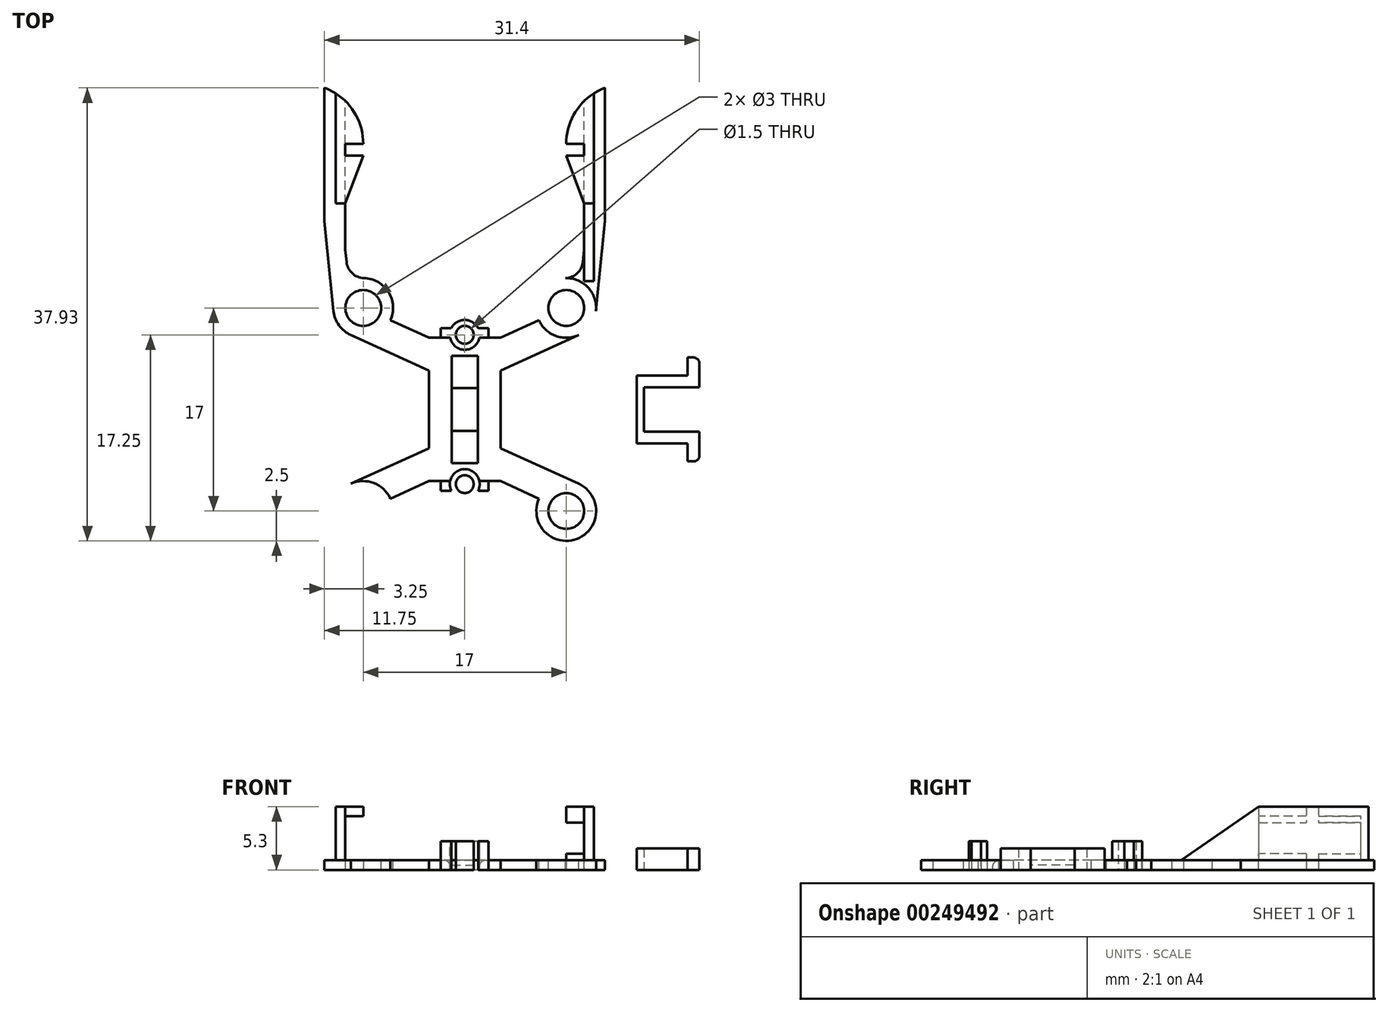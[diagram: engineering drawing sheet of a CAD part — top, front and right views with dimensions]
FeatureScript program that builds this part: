
annotation { "Feature Type Name" : "Feature", "Feature Type Description" : "" }
export const myFeature = defineFeature(function(context is Context, id is Id, definition is map)
    precondition{}
    {
        {
            var Q0;
            Q0=qCreatedBy(makeId("Top.planeOp"),FACE);
            var sketch = newSketch(context, id + "F0", { "sketchPlane" : qUnion([Q0])});
            skLineSegment(sketch, "E0", {"start": v(0, 24.7) * mm, "end": v(0, -21.3) * mm, "construction": true});
            skLineSegment(sketch, "E1", {"start": v(-15, 1.7) * mm, "end": v(15, 1.7) * mm, "construction": true});
            skCircle(sketch, "E2", {"center": v(0, 7.95) * mm, "radius": 1.25 * mm});
            skPoint(sketch, "E3", {"position": v(0, 1.7) * mm});
            skLineSegment(sketch, "E4.bottom", {"start": v(-8.5, 10.2) * mm, "end": v(8.5, 10.2) * mm, "construction": true});
            skLineSegment(sketch, "E4.top", {"start": v(-8.5, -6.8) * mm, "end": v(8.5, -6.8) * mm, "construction": true});
            skLineSegment(sketch, "E4.left", {"start": v(-8.5, 10.2) * mm, "end": v(-8.5, -6.8) * mm, "construction": true});
            skLineSegment(sketch, "E4.right", {"start": v(8.5, 10.2) * mm, "end": v(8.5, -6.8) * mm, "construction": true});
            skPoint(sketch, "E5.positionSnap0", {"position": v(0, 10.2) * mm});
            skPoint(sketch, "E5.positionSnap1", {"position": v(-8.5, 1.7) * mm});
            skArc(sketch, "E6", {"start": v(-6.22, 9.17) * mm, "mid": v(-9.38, 12.54) * mm, "end": v(-9.53, 7.92) * mm});
            skCircle(sketch, "E7", {"center": v(-8.5, 10.2) * mm, "radius": 1.5 * mm});
            skCircle(sketch, "E8", {"center": v(0, 7.95) * mm, "radius": 0.75 * mm});
            skLineSegment(sketch, "E9.bottom", {"start": v(-3, 7.7) * mm, "end": v(-1.22, 7.7) * mm});
            skLineSegment(sketch, "E9.top", {"start": v(-3, -4.3) * mm, "end": v(-1.22, -4.3) * mm});
            skLineSegment(sketch, "E9.left", {"start": v(-3, 4.95) * mm, "end": v(-3, -1.55) * mm});
            skLineSegment(sketch, "E9.right", {"start": v(3, 4.95) * mm, "end": v(3, -1.55) * mm});
            skPoint(sketch, "E10.positionSnap0", {"position": v(0, 7.7) * mm});
            skPoint(sketch, "E10.positionSnap1", {"position": v(-3, 1.7) * mm});
            skLineSegment(sketch, "E11", {"start": v(-9.53, 7.92) * mm, "end": v(-3, 4.95) * mm});
            skLineSegment(sketch, "E12.trimOffspring", {"start": v(-6.22, 9.17) * mm, "end": v(-3, 7.7) * mm});
            skLineSegment(sketch, "E13.trimOffspring", {"start": v(1.22, 7.7) * mm, "end": v(3, 7.7) * mm});
            skLineSegment(sketch, "E14.bottom", {"start": v(-1.1, 6.2) * mm, "end": v(1.1, 6.2) * mm});
            skLineSegment(sketch, "E14.top", {"start": v(-1.1, -2.8) * mm, "end": v(1.1, -2.8) * mm});
            skLineSegment(sketch, "E14.left", {"start": v(-1.1, 6.2) * mm, "end": v(-1.1, -2.8) * mm});
            skLineSegment(sketch, "E14.right", {"start": v(1.1, 6.2) * mm, "end": v(1.1, -2.8) * mm});
            skPoint(sketch, "E15.positionSnap0", {"position": v(0, 6.2) * mm});
            skPoint(sketch, "E15.positionSnap1", {"position": v(-1.1, 1.7) * mm});
            skCircle(sketch, "E16.MirrorC", {"center": v(8.5, 10.2) * mm, "radius": 1.5 * mm});
            skArc(sketch, "E17.MirrorCS", {"start": v(6.22, 9.17) * mm, "mid": v(9.38, 12.54) * mm, "end": v(9.53, 7.92) * mm});
            skLineSegment(sketch, "E18.MirrorCS", {"start": v(9.53, 7.92) * mm, "end": v(3, 4.95) * mm});
            skLineSegment(sketch, "E19.MirrorCS", {"start": v(6.22, 9.17) * mm, "end": v(3, 7.7) * mm});
            skArc(sketch, "E20.MirrorCS", {"start": v(-6.22, -5.77) * mm, "mid": v(-9.38, -9.14) * mm, "end": v(-9.53, -4.52) * mm});
            skCircle(sketch, "E21.MirrorC", {"center": v(-8.5, -6.8) * mm, "radius": 1.5 * mm});
            skLineSegment(sketch, "E22.MirrorCS", {"start": v(-9.53, -4.52) * mm, "end": v(-3, -1.55) * mm});
            skLineSegment(sketch, "E23.MirrorCS", {"start": v(-6.22, -5.77) * mm, "end": v(-3, -4.3) * mm});
            skLineSegment(sketch, "E24.MirrorCS", {"start": v(6.22, -5.77) * mm, "end": v(3, -4.3) * mm});
            skLineSegment(sketch, "E25.MirrorCS", {"start": v(9.53, -4.52) * mm, "end": v(3, -1.55) * mm});
            skArc(sketch, "E26.MirrorCS", {"start": v(6.22, -5.77) * mm, "mid": v(9.38, -9.14) * mm, "end": v(9.53, -4.52) * mm});
            skCircle(sketch, "E27.MirrorC", {"center": v(8.5, -6.8) * mm, "radius": 1.5 * mm});
            skCircle(sketch, "E28.MirrorC", {"center": v(0, -4.55) * mm, "radius": 0.75 * mm});
            skCircle(sketch, "E29.MirrorC", {"center": v(0, -4.55) * mm, "radius": 1.25 * mm});
            skLineSegment(sketch, "E30.MirrorCS", {"start": v(1.22, -4.3) * mm, "end": v(3, -4.3) * mm});
            skLineSegment(sketch, "E31", {"start": v(-2, 8.5) * mm, "end": v(-1.12, 8.5) * mm});
            skLineSegment(sketch, "E32", {"start": v(-2, 8.5) * mm, "end": v(-2, 7.7) * mm});
            skLineSegment(sketch, "E33.MirrorCS", {"start": v(2, 8.5) * mm, "end": v(2, 7.7) * mm});
            skLineSegment(sketch, "E34.MirrorCS", {"start": v(2, 8.5) * mm, "end": v(1.12, 8.5) * mm});
            skLineSegment(sketch, "E35.MirrorCS", {"start": v(-2, -5.1) * mm, "end": v(-2, -4.3) * mm});
            skLineSegment(sketch, "E36.MirrorCS", {"start": v(-2, -5.1) * mm, "end": v(-1.12, -5.1) * mm});
            skLineSegment(sketch, "E37.MirrorCS", {"start": v(2, -5.1) * mm, "end": v(1.12, -5.1) * mm});
            skLineSegment(sketch, "E38.MirrorCS", {"start": v(2, -5.1) * mm, "end": v(2, -4.3) * mm});
            skArc(sketch, "E39", {"start": v(-6.22, 9.17) * mm, "mid": v(-8.6, 7.7) * mm, "end": v(-10.86, 9.36) * mm});
            skArc(sketch, "E40.MirrorCS", {"start": v(6.22, 9.17) * mm, "mid": v(8.6, 7.7) * mm, "end": v(10.86, 9.36) * mm});
            skArc(sketch, "E41.MirrorCS", {"start": v(-6.22, -5.77) * mm, "mid": v(-8.6, -4.3) * mm, "end": v(-10.86, -5.96) * mm});
            skArc(sketch, "E42.MirrorCS", {"start": v(6.22, -5.77) * mm, "mid": v(8.6, -4.3) * mm, "end": v(10.86, -5.96) * mm});
            skLineSegment(sketch, "E43", {"start": v(-1.1, 3.5) * mm, "end": v(1.1, 3.5) * mm});
            skLineSegment(sketch, "E44.MirrorCS", {"start": v(-1.1, -0.1) * mm, "end": v(1.1, -0.1) * mm});
            skLineSegment(sketch, "E45", {"start": v(15, 1.7) * mm, "end": v(15, 3.55) * mm});
            skLineSegment(sketch, "E46", {"start": v(15, 3.55) * mm, "end": v(19.65, 3.55) * mm});
            skLineSegment(sketch, "E47", {"start": v(19.65, 3.55) * mm, "end": v(19.65, 5.55) * mm});
            skLineSegment(sketch, "E48", {"start": v(19.15, 6.05) * mm, "end": v(18.65, 6.05) * mm});
            skLineSegment(sketch, "E49", {"start": v(18.65, 6.05) * mm, "end": v(18.65, 4.55) * mm});
            skLineSegment(sketch, "E50", {"start": v(18.65, 4.55) * mm, "end": v(14.4, 4.55) * mm});
            skLineSegment(sketch, "E51", {"start": v(14.4, 4.55) * mm, "end": v(14.4, 1.7) * mm});
            skPoint(sketch, "E52.visualSharp", {"position": v(19.65, 6.05) * mm});
            skArc(sketch, "E52.filletArc", {"start": v(19.65, 5.55) * mm, "mid": v(19.5, 5.9) * mm, "end": v(19.15, 6.05) * mm});
            skLineSegment(sketch, "E53.MirrorCS", {"start": v(14.4, -1.15) * mm, "end": v(14.4, 1.7) * mm});
            skLineSegment(sketch, "E54.MirrorCS", {"start": v(15, 1.7) * mm, "end": v(15, -0.15) * mm});
            skLineSegment(sketch, "E55.MirrorCS", {"start": v(15, -0.15) * mm, "end": v(19.65, -0.15) * mm});
            skLineSegment(sketch, "E56.MirrorCS", {"start": v(18.65, -1.15) * mm, "end": v(14.4, -1.15) * mm});
            skLineSegment(sketch, "E57.MirrorCS", {"start": v(18.65, -2.65) * mm, "end": v(18.65, -1.15) * mm});
            skLineSegment(sketch, "E58.MirrorCS", {"start": v(19.15, -2.65) * mm, "end": v(18.65, -2.65) * mm});
            skArc(sketch, "E59.MirrorCS", {"start": v(19.65, -2.15) * mm, "mid": v(19.5, -2.5) * mm, "end": v(19.15, -2.65) * mm});
            skLineSegment(sketch, "E60.MirrorCS", {"start": v(19.65, -0.15) * mm, "end": v(19.65, -2.15) * mm});
            skLineSegment(sketch, "E61", {"start": v(-11.75, 17.45) * mm, "end": v(-10.99, 9.95) * mm});
            skLineSegment(sketch, "E62", {"start": v(-10, 15.07) * mm, "end": v(-10, 18.95) * mm});
            skLineSegment(sketch, "E63", {"start": v(-10, 18.95) * mm, "end": v(-8.5, 22.95) * mm});
            skLineSegment(sketch, "E64", {"start": v(-8.5, 22.95) * mm, "end": v(-10, 22.95) * mm});
            skLineSegment(sketch, "E65", {"start": v(-10, 22.95) * mm, "end": v(-10, 23.95) * mm});
            skLineSegment(sketch, "E66", {"start": v(-10, 23.95) * mm, "end": v(-8.5, 23.95) * mm});
            skLineSegment(sketch, "E67", {"start": v(-11.75, 28.63) * mm, "end": v(-11.75, 17.45) * mm});
            skLineSegment(sketch, "E68", {"start": v(-10, 15.07) * mm, "end": v(-9.9, 14.05) * mm});
            skArc(sketch, "E69", {"start": v(-9.9, 14.05) * mm, "mid": v(-9.42, 13.1) * mm, "end": v(-8.44, 12.7) * mm});
            skArc(sketch, "E70", {"start": v(-8.5, 23.95) * mm, "mid": v(-9.4, 26.8) * mm, "end": v(-11.75, 28.63) * mm});
            skLineSegment(sketch, "E71", {"start": v(-10, 18.95) * mm, "end": v(-10, 22.95) * mm});
            skLineSegment(sketch, "E72", {"start": v(-10, 23.95) * mm, "end": v(-10, 27.52) * mm});
            skArc(sketch, "E73.MirrorCS", {"start": v(8.5, 23.95) * mm, "mid": v(9.4, 26.8) * mm, "end": v(11.75, 28.63) * mm});
            skLineSegment(sketch, "E74.MirrorCS", {"start": v(11.75, 28.63) * mm, "end": v(11.75, 17.45) * mm});
            skLineSegment(sketch, "E75.MirrorCS", {"start": v(10, 23.95) * mm, "end": v(10, 27.52) * mm});
            skLineSegment(sketch, "E76.MirrorCS", {"start": v(10, 23.95) * mm, "end": v(8.5, 23.95) * mm});
            skLineSegment(sketch, "E77.MirrorCS", {"start": v(10, 22.95) * mm, "end": v(10, 23.95) * mm});
            skLineSegment(sketch, "E78.MirrorCS", {"start": v(8.5, 22.95) * mm, "end": v(10, 22.95) * mm});
            skLineSegment(sketch, "E79.MirrorCS", {"start": v(10, 18.95) * mm, "end": v(8.5, 22.95) * mm});
            skLineSegment(sketch, "E80.MirrorCS", {"start": v(10, 18.95) * mm, "end": v(10, 22.95) * mm});
            skLineSegment(sketch, "E81.MirrorCS", {"start": v(10, 15.07) * mm, "end": v(10, 18.95) * mm});
            skLineSegment(sketch, "E82.MirrorCS", {"start": v(10, 15.07) * mm, "end": v(9.9, 14.05) * mm});
            skArc(sketch, "E83.MirrorCS", {"start": v(9.9, 14.05) * mm, "mid": v(9.42, 13.1) * mm, "end": v(8.44, 12.7) * mm});
            skLineSegment(sketch, "E84.MirrorCS", {"start": v(11.75, 17.45) * mm, "end": v(10.99, 9.95) * mm});
            skLineSegment(sketch, "E85", {"start": v(10.8, 28.16) * mm, "end": v(10.8, 18.95) * mm});
            skLineSegment(sketch, "E86", {"start": v(10.8, 18.95) * mm, "end": v(10, 18.95) * mm});
            skLineSegment(sketch, "E87.MirrorCS", {"start": v(-10.8, 18.95) * mm, "end": v(-10, 18.95) * mm});
            skLineSegment(sketch, "E88.MirrorCS", {"start": v(-10.8, 28.16) * mm, "end": v(-10.8, 18.95) * mm});
            skSolve(sketch);
        }
        {
            var Q0;
            Q0=makeQuery(id+"F0.imprint","IMPRINT",FACE,{"disambiguationData":[TD([[makeQuery(id+"F0.imprint","IMPRINT",EDGE,{"derivedFrom":sQuery(id+"F0.wireOp",EDGE,"E9.left")}),1.0]])]});
            var Q1;
            {var subQ10=sQuery(id+"F0.wireOp",EDGE,"E12.trimOffspring");Q1=makeQuery(id+"F0.imprint","IMPRINT",FACE,{"disambiguationData":[TD([[makeQuery(id+"F0.imprint","IMPRINT",EDGE,{"derivedFrom":subQ10}),1.0]])]});}
            var Q2;
            {var subQ0=sQuery(id+"F0.wireOp",EDGE,"E43");Q2=makeQuery(id+"F0.imprint","IMPRINT",FACE,{"disambiguationData":[TD([[makeQuery(id+"F0.imprint","IMPRINT",EDGE,{"derivedFrom":subQ0}),-1.0]])]});}
            extrude(context, id + "F1", {"entities" : qUnion([Q0, Q1, Q2]), "oppositeDirection" : true, "depth" : .8 * mm});
        }
        {
            var Q0;
            {var subQ3=sQuery(id+"F0.wireOp",EDGE,"E31");Q0=makeQuery(id+"F0.imprint","IMPRINT",FACE,{"disambiguationData":[TD([[makeQuery(id+"F0.imprint","IMPRINT",EDGE,{"derivedFrom":subQ3}),-1.0]])]});}
            var Q1;
            Q1=makeQuery(id+"F0.imprint","IMPRINT",FACE,{"disambiguationData":[TD([[makeQuery(id+"F0.imprint","IMPRINT",EDGE,{"derivedFrom":sQuery(id+"F0.wireOp",EDGE,"E8")}),-1.0]])]});
            var Q2;
            {var subQ4=sQuery(id+"F0.wireOp",EDGE,"E33.MirrorCS");Q2=makeQuery(id+"F0.imprint","IMPRINT",FACE,{"disambiguationData":[TD([[makeQuery(id+"F0.imprint","IMPRINT",EDGE,{"derivedFrom":subQ4}),-1.0]])]});}
            var Q3;
            {var subQ3=sQuery(id+"F0.wireOp",EDGE,"E35.MirrorCS");Q3=makeQuery(id+"F0.imprint","IMPRINT",FACE,{"disambiguationData":[TD([[makeQuery(id+"F0.imprint","IMPRINT",EDGE,{"derivedFrom":subQ3}),-1.0]])]});}
            var Q4;
            Q4=makeQuery(id+"F0.imprint","IMPRINT",FACE,{"disambiguationData":[TD([[makeQuery(id+"F0.imprint","IMPRINT",EDGE,{"derivedFrom":sQuery(id+"F0.wireOp",EDGE,"E28.MirrorC")}),1.0]])]});
            var Q5;
            {var subQ3=sQuery(id+"F0.wireOp",EDGE,"E37.MirrorCS");Q5=makeQuery(id+"F0.imprint","IMPRINT",FACE,{"disambiguationData":[TD([[makeQuery(id+"F0.imprint","IMPRINT",EDGE,{"derivedFrom":subQ3}),-1.0]])]});}
            extrude(context, id + "F2", {"entities" : qUnion([Q0, Q1, Q2, Q3, Q4, Q5]), "operationType" : NewBodyOperationType.ADD, "depth" : 1.6 * mm, "hasSecondDirection" : true, "secondDirectionOppositeDirection" : true, "secondDirectionDepth" : .8 * mm});
        }
        {
            var Q0;
            {var subQ0=sQuery(id+"F0.wireOp",EDGE,"E43");Q0=makeQuery(id+"F0.imprint","IMPRINT",FACE,{"disambiguationData":[TD([[makeQuery(id+"F0.imprint","IMPRINT",EDGE,{"derivedFrom":subQ0}),-1.0]])]});}
            extrude(context, id + "F3", {"entities" : qUnion([Q0]), "operationType" : NewBodyOperationType.REMOVE, "oppositeDirection" : true, "depth" : .4 * mm});
        }
        {
            var Q0;
            {var subQ0=sQuery(id+"F0.wireOp",EDGE,"E6");Q0=makeQuery(id+"F0.imprint","IMPRINT",FACE,{"disambiguationData":[TD([[makeQuery(id+"F0.imprint","IMPRINT",EDGE,{"derivedFrom":subQ0}),1.0]])]});}
            var Q1;
            Q1=makeQuery(id+"F0.imprint","IMPRINT",FACE,{"disambiguationData":[TD([[makeQuery(id+"F0.imprint","IMPRINT",EDGE,{"derivedFrom":sQuery(id+"F0.wireOp",EDGE,"E16.MirrorC")}),1.0]])]});
            var Q2;
            {var subQ0=sQuery(id+"F0.wireOp",EDGE,"E20.MirrorCS");Q2=makeQuery(id+"F0.imprint","IMPRINT",FACE,{"disambiguationData":[TD([[makeQuery(id+"F0.imprint","IMPRINT",EDGE,{"derivedFrom":subQ0}),-1.0]])]});}
            var Q3;
            {var subQ0=sQuery(id+"F0.wireOp",EDGE,"E26.MirrorCS");Q3=makeQuery(id+"F0.imprint","IMPRINT",FACE,{"disambiguationData":[TD([[makeQuery(id+"F0.imprint","IMPRINT",EDGE,{"derivedFrom":subQ0}),1.0]])]});}
            var Q4;
            {var subQ2=sQuery(id+"F0.wireOp",EDGE,"E61");Q4=makeQuery(id+"F0.imprint","IMPRINT",FACE,{"disambiguationData":[TD([[makeQuery(id+"F0.imprint","IMPRINT",EDGE,{"derivedFrom":subQ2}),1.0]])]});}
            var Q5;
            Q5=makeQuery(id+"F0.imprint","IMPRINT",FACE,{"disambiguationData":[TD([[makeQuery(id+"F0.imprint","IMPRINT",EDGE,{"derivedFrom":sQuery(id+"F0.wireOp",EDGE,"E81.MirrorCS")}),-1.0]])]});
            extrude(context, id + "F4", {"entities" : qUnion([Q0, Q1, Q2, Q3, Q4, Q5]), "operationType" : NewBodyOperationType.ADD, "oppositeDirection" : true, "depth" : .8 * mm});
        }
        {
            var Q0;
            Q0=makeQuery(id+"F0.imprint","IMPRINT",FACE,{"disambiguationData":[TD([[makeQuery(id+"F0.imprint","IMPRINT",EDGE,{"derivedFrom":sQuery(id+"F0.wireOp",EDGE,"E65")}),1.0]])]});
            var Q1;
            Q1=makeQuery(id+"F0.imprint","IMPRINT",FACE,{"disambiguationData":[TD([[makeQuery(id+"F0.imprint","IMPRINT",EDGE,{"derivedFrom":sQuery(id+"F0.wireOp",EDGE,"E63")}),1.0]])]});
            var Q2;
            {var subQ0=sQuery(id+"F0.wireOp",EDGE,"E66");Q2=makeQuery(id+"F0.imprint","IMPRINT",FACE,{"disambiguationData":[TD([[makeQuery(id+"F0.imprint","IMPRINT",EDGE,{"derivedFrom":subQ0}),1.0]])]});}
            var Q3;
            {var subQ0=sQuery(id+"F0.wireOp",EDGE,"E75.MirrorCS");Q3=makeQuery(id+"F0.imprint","IMPRINT",FACE,{"disambiguationData":[TD([[makeQuery(id+"F0.imprint","IMPRINT",EDGE,{"derivedFrom":subQ0}),-1.0]])]});}
            var Q4;
            Q4=makeQuery(id+"F0.imprint","IMPRINT",FACE,{"disambiguationData":[TD([[makeQuery(id+"F0.imprint","IMPRINT",EDGE,{"derivedFrom":sQuery(id+"F0.wireOp",EDGE,"E78.MirrorCS")}),-1.0]])]});
            var Q5;
            {var subQ2=sQuery(id+"F0.wireOp",EDGE,"E75.MirrorCS");Q5=makeQuery(id+"F0.imprint","IMPRINT",FACE,{"disambiguationData":[TD([[makeQuery(id+"F0.imprint","IMPRINT",EDGE,{"derivedFrom":subQ2}),1.0]])]});}
            extrude(context, id + "F5", {"entities" : qUnion([Q0, Q1, Q2, Q3, Q4, Q5]), "operationType" : NewBodyOperationType.ADD, "depth" : 4.5 * mm, "hasSecondDirection" : true, "secondDirectionOppositeDirection" : true, "secondDirectionDepth" : .8 * mm});
        }
        {
            var Q0;
            Q0=makeQuery(id+"F5.opExtrude","SWEPT_FACE",FACE,{"disambiguationData":[OSD([sQuery(id+"F0.wireOp",EDGE,"E64")])]});
            var sketch = newSketch(context, id + "F6", { "sketchPlane" : qUnion([Q0])});
            skLineSegment(sketch, "E89", {"start": v(8.42, 1.85) * mm, "end": v(-15.72, 1.85) * mm, "construction": true});
            skPoint(sketch, "E89.startSnap0", {"position": v(10, 1.85) * mm});
            skPoint(sketch, "E89.endSnap0", {"position": v(10, 1.85) * mm});
            skLineSegment(sketch, "E90", {"start": v(8.5, 3.7) * mm, "end": v(10, 3.7) * mm});
            skLineSegment(sketch, "E91", {"start": v(10, 3.7) * mm, "end": v(10, 0) * mm});
            skLineSegment(sketch, "E92", {"start": v(10, 0) * mm, "end": v(8.5, 0) * mm});
            skLineSegment(sketch, "E93", {"start": v(-8.5, 3.15) * mm, "end": v(-10, 3.15) * mm});
            skLineSegment(sketch, "E94", {"start": v(-10, 0.55) * mm, "end": v(-8.5, 0.55) * mm});
            skLineSegment(sketch, "E95", {"start": v(8.5, 3.7) * mm, "end": v(8.5, 0) * mm});
            skLineSegment(sketch, "E96.0.1", {"start": v(-8.5, 0.55) * mm, "end": v(-8.5, 3.15) * mm});
            skLineSegment(sketch, "E96.0.3", {"start": v(-10, 3.15) * mm, "end": v(-10, 0.55) * mm});
            skPoint(sketch, "E97.orphan", {"position": v(-8.5, 4.5) * mm});
            skPoint(sketch, "E98.orphan", {"position": v(-10, 4.5) * mm});
            skPoint(sketch, "E99.orphan", {"position": v(-10, -0.8) * mm});
            skPoint(sketch, "E100.orphan", {"position": v(-8.5, -0.8) * mm});
            skSolve(sketch);
        }
        {
            var Q0;
            Q0 = qSketchRegion(id + "F6", true);
            extrude(context, id + "F7", {"entities" : qUnion([Q0]), "operationType" : NewBodyOperationType.REMOVE, "oppositeDirection" : true, "depth" : 25 * mm, "hasSecondDirection" : true, "secondDirectionOppositeDirection" : false, "secondDirectionDepth" : 25 * mm});
        }
        {
            var Q0;
            Q0=makeQuery(id+"F7.boolean.opBoolean","MERGE",FACE,{"derivedFrom":[makeQuery(id+"F5.opExtrude","SWEPT_FACE",FACE,{"disambiguationData":[OSD([sQuery(id+"F0.wireOp",EDGE,"E77.MirrorCS")])]}),makeQuery(id+"F7.opExtrude","SWEPT_FACE",FACE,{"disambiguationData":[OSD([sQuery(id+"F6.wireOp",EDGE,"E96.0.3")])]})]});
            var sketch = newSketch(context, id + "F8", { "sketchPlane" : qUnion([Q0])});
            skLineSegment(sketch, "E101", {"start": v(-18.95, 4.5) * mm, "end": v(-18.95, 0) * mm});
            skLineSegment(sketch, "E102", {"start": v(-18.95, 4.5) * mm, "end": v(-12.45, 0) * mm});
            skLineSegment(sketch, "E103", {"start": v(-12.45, 0) * mm, "end": v(-18.95, 0) * mm});
            skSolve(sketch);
        }
        {
            var Q0;
            Q0 = qSketchRegion(id + "F8", true);
            extrude(context, id + "F9", {"entities" : qUnion([Q0]), "operationType" : NewBodyOperationType.ADD, "oppositeDirection" : true, "depth" : .8 * mm});
        }
        {
            var Q0;
            Q0=makeQuery(id+"F0.imprint","IMPRINT",FACE,{"disambiguationData":[TD([[makeQuery(id+"F0.imprint","IMPRINT",EDGE,{"derivedFrom":sQuery(id+"F0.wireOp",EDGE,"E45")}),1.0]])]});
            extrude(context, id + "F10", {"entities" : qUnion([Q0]), "depth" : 1 * mm, "hasSecondDirection" : true, "secondDirectionOppositeDirection" : true, "secondDirectionDepth" : .8 * mm});
        }
        {
            var Q0;
            Q0=makeQuery(id+"F1.opExtrude","CAP_EDGE",EDGE,{"disambiguationData":[OSD([sQuery(id+"F0.wireOp",EDGE,"E2")])],"isStart":true});
            var Q1;
            Q1=makeQuery(id+"F1.opExtrude","CAP_EDGE",EDGE,{"disambiguationData":[OSD([sQuery(id+"F0.wireOp",EDGE,"E29.MirrorC")])],"isStart":true});
            fillet(context, id + "F11", {"entities" : qUnion([Q0, Q1]), "radius" : .5 * mm, "tangentPropagation" : true, "allowEdgeOverflow" : false});
        }
    });
